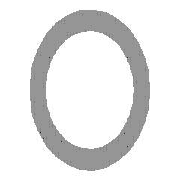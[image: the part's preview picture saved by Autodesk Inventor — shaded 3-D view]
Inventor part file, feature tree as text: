
AUTODESK INVENTOR PART (.ipt)
format: ipt  version: 2013 (Build 170138000, 138)  size: 108,544 bytes
history: native  units: mm (DEFAULTED — no unit token found)
features: other x4, sketch x3, plane x1
ambient origin geometry x8: Origin, YZ Plane, XZ Plane, XY Plane, X Axis, Y Axis, Z Axis, Center Point
bodies: Solid1 (feature_tree), Body (feature_tree)
feature tree (8):
  parser-record x1  (decoder bookkeeping rows leaked as tree rows — omitted from the tree; the rows remain in map.json)
  other  "Driven Length"
  other  "Start plane"
  other  "End plane"
  sketch  "Sketch"  dims[d2=457.2mm d3=0.0mm d4=-0.0mm d5=457.2mm d6=90.0deg d7=457.2mm]
  sketch  "Sketch3"  dims[d0=33.401mm]
  plane  "Work Plane3"
  sketch  "Sketch4"  dims[d1=3.3782mm]
